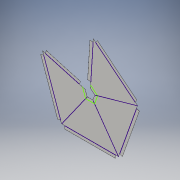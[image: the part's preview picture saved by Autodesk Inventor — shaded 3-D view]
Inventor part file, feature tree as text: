
AUTODESK INVENTOR PART (.ipt)
format: ipt  version: 2016 (Build 200138000, 138)  size: 197,120 bytes
history: native  units: in
note: dims shown in document units (in); Inventor stores cm internally (conversion verified against a paired STEP export)
features: sketch x3, extrude x2
ambient origin geometry x8: Origin, YZ Plane, XZ Plane, XY Plane, X Axis, Y Axis, Z Axis, Center Point
bodies: Body1 (feature_tree)
feature tree (5):
  extrude  "Extrusion2"  Depth=3.7402in
  extrude  "Extrusion3"  Depth=2.227in
  sketch  "Sketch3"  dims[d4=2.7276in d16=0.591in d17=0.591in d18=0.591in d19=3.74in d20=2.728in d21=3.74in d22=2.728in d23=3.74in d24=2.728in d25=0.005in d26=0.0in d34=0.2in d35=0.2in d38=0.2in d39=0.2in d42=0.2in d43=0.2in d46=0.2in d47=0.2in d50=0.2in d51=0.2in d56=0.2in d58=0.2in d64=0.3761in d65=0.15in d66=0.3761in d67=0.15in d68=0.3761in d69=0.15in d70=0.3761in d71=0.15in d72=0.3761in d73=0.15in d74=0.005in d75=0.0in d76=0.2in]
  sketch  "Sketch1"  dims[d0=2.7276in d1=3.7402in]
  sketch  "Sketch2"  dims[d2=0.5906in d3=2.227in]
